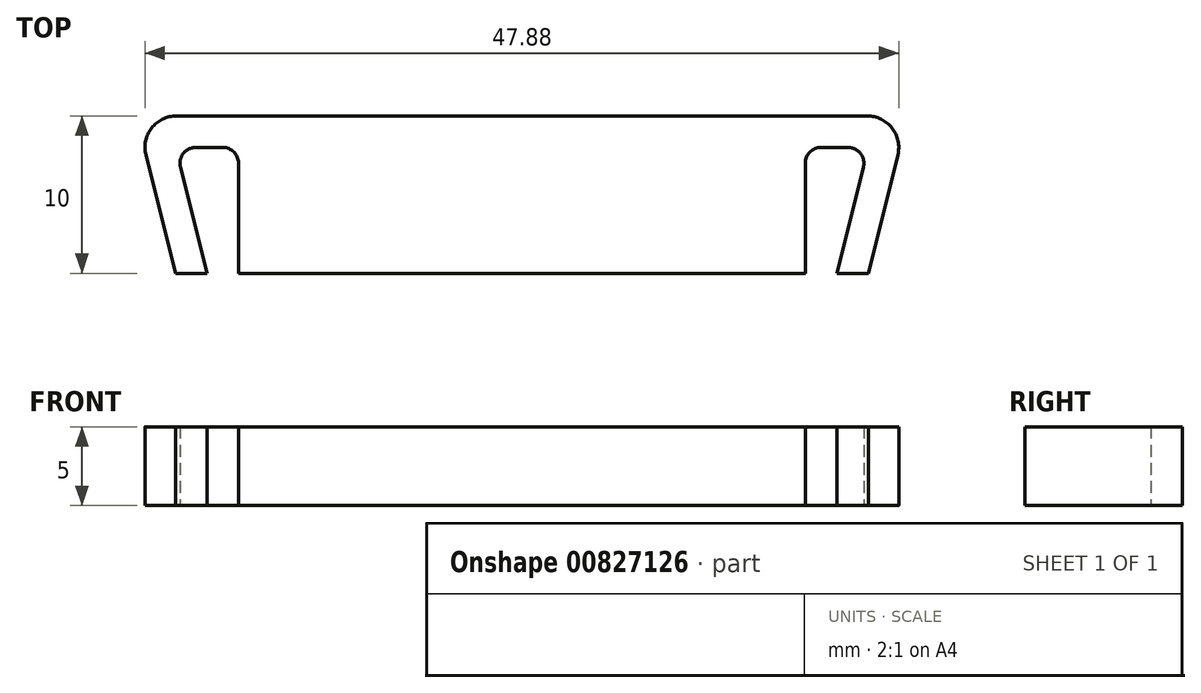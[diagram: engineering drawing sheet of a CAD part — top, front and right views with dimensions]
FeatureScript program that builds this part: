
annotation { "Feature Type Name" : "Feature", "Feature Type Description" : "" }
export const myFeature = defineFeature(function(context is Context, id is Id, definition is map)
    precondition{}
    {
        {
            var Q0;
            Q0=qCreatedBy(makeId("Top.planeOp"),FACE);
            var sketch = newSketch(context, id + "F0", { "sketchPlane" : qUnion([Q0])});
            skLineSegment(sketch, "E0", {"start": v(0, 0) * mm, "end": v(-18, 0) * mm});
            skLineSegment(sketch, "E1", {"start": v(-18, 0) * mm, "end": v(-18, 7) * mm});
            skLineSegment(sketch, "E2", {"start": v(-19, 8) * mm, "end": v(-20.72, 8) * mm});
            skLineSegment(sketch, "E3", {"start": v(-21.69, 6.76) * mm, "end": v(-20, 0) * mm});
            skLineSegment(sketch, "E4", {"start": v(-20, 0) * mm, "end": v(-22, 0) * mm});
            skLineSegment(sketch, "E5", {"start": v(-22, 0) * mm, "end": v(-23.88, 7.51) * mm});
            skLineSegment(sketch, "E6", {"start": v(-21.94, 10) * mm, "end": v(21.94, 10) * mm});
            skLineSegment(sketch, "E7", {"start": v(23.88, 7.51) * mm, "end": v(22, 0) * mm});
            skLineSegment(sketch, "E8", {"start": v(22, 0) * mm, "end": v(20, 0) * mm});
            skLineSegment(sketch, "E9", {"start": v(20, 0) * mm, "end": v(21.69, 6.76) * mm});
            skLineSegment(sketch, "E10", {"start": v(20.72, 8) * mm, "end": v(19, 8) * mm});
            skLineSegment(sketch, "E11", {"start": v(18, 7) * mm, "end": v(18, 0) * mm});
            skLineSegment(sketch, "E12", {"start": v(18, 0) * mm, "end": v(0, 0) * mm});
            skLineSegment(sketch, "E13", {"start": v(24.5, 10) * mm, "end": v(24.5, 0) * mm, "construction": true});
            skLineSegment(sketch, "E14", {"start": v(-24.5, 10) * mm, "end": v(-24.5, 0) * mm, "construction": true});
            skLineSegment(sketch, "E15", {"start": v(-20, 0) * mm, "end": v(-18, 0) * mm, "construction": true});
            skLineSegment(sketch, "E16", {"start": v(18, 0) * mm, "end": v(20, 0) * mm, "construction": true});
            skPoint(sketch, "E17.visualSharp", {"position": v(-24.5, 10) * mm});
            skArc(sketch, "E17.filletArc", {"start": v(-21.94, 10) * mm, "mid": v(-23.51, 9.23) * mm, "end": v(-23.88, 7.51) * mm});
            skPoint(sketch, "E18.visualSharp", {"position": v(24.5, 10) * mm});
            skArc(sketch, "E18.filletArc", {"start": v(23.88, 7.51) * mm, "mid": v(23.51, 9.23) * mm, "end": v(21.94, 10) * mm});
            skPoint(sketch, "E19.visualSharp", {"position": v(22, 8) * mm});
            skArc(sketch, "E19.filletArc", {"start": v(21.69, 6.76) * mm, "mid": v(21.5, 7.62) * mm, "end": v(20.72, 8) * mm});
            skPoint(sketch, "E20.visualSharp", {"position": v(-22, 8) * mm});
            skArc(sketch, "E20.filletArc", {"start": v(-20.72, 8) * mm, "mid": v(-21.5, 7.62) * mm, "end": v(-21.69, 6.76) * mm});
            skPoint(sketch, "E21.visualSharp", {"position": v(-18, 8) * mm});
            skArc(sketch, "E21.filletArc", {"start": v(-18, 7) * mm, "mid": v(-18.3, 7.7) * mm, "end": v(-19, 8) * mm});
            skPoint(sketch, "E22.visualSharp", {"position": v(18, 8) * mm});
            skArc(sketch, "E22.filletArc", {"start": v(19, 8) * mm, "mid": v(18.3, 7.7) * mm, "end": v(18, 7) * mm});
            skSolve(sketch);
        }
        {
            var Q0;
            Q0=makeQuery(id+"F0.imprint","IMPRINT",FACE,{"disambiguationData":[TD([[makeQuery(id+"F0.imprint","IMPRINT",EDGE,{"derivedFrom":sQuery(id+"F0.wireOp",EDGE,"E0")}),-1.0]])]});
            extrude(context, id + "F1", {"entities" : qUnion([Q0]), "depth" : 5 * mm, "offsetDistance" : 25 * mm});
        }
    });
